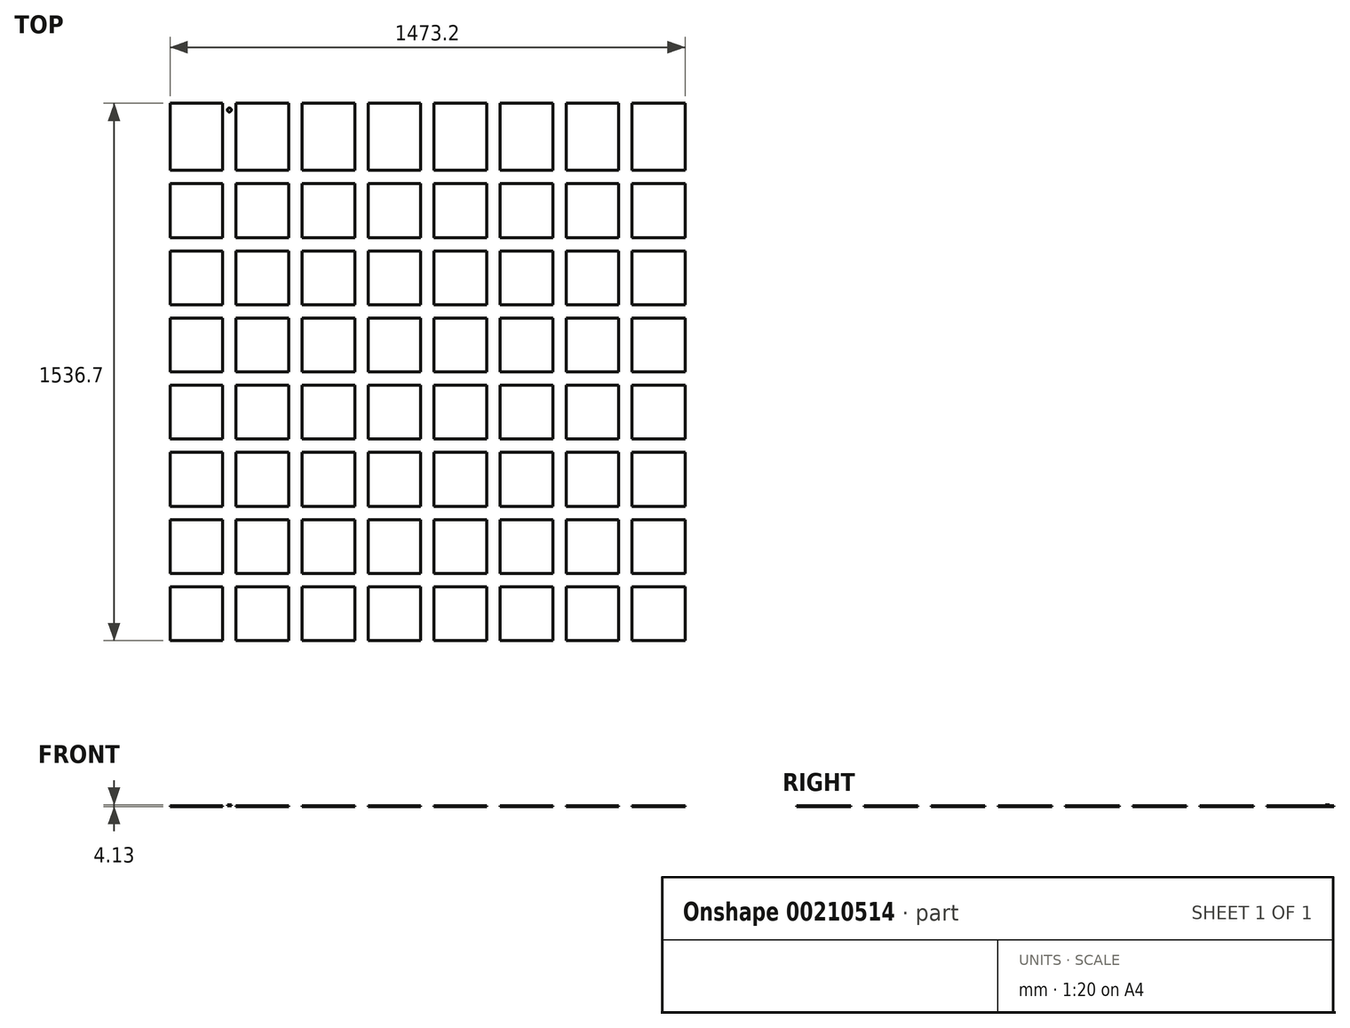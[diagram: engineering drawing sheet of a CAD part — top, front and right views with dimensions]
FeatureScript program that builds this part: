
annotation { "Feature Type Name" : "Feature", "Feature Type Description" : "" }
export const myFeature = defineFeature(function(context is Context, id is Id, definition is map)
    precondition{}
    {
        {
            var Q0;
            Q0=qCreatedBy(makeId("Top.planeOp"),FACE);
            var sketch = newSketch(context, id + "F0", { "sketchPlane" : qUnion([Q0])});
            skLineSegment(sketch, "E0.bottom", {"start": v(-755.65, 787.4) * mm, "end": v(755.65, 787.4) * mm});
            skLineSegment(sketch, "E0.top", {"start": v(-755.65, -787.4) * mm, "end": v(755.65, -787.4) * mm});
            skLineSegment(sketch, "E0.left", {"start": v(-755.65, 787.4) * mm, "end": v(-755.65, -787.4) * mm});
            skLineSegment(sketch, "E0.right", {"start": v(755.65, 787.4) * mm, "end": v(755.65, -787.4) * mm});
            skPoint(sketch, "E0.middle", {"position": v(0, 0) * mm});
            skSolve(sketch);
        }
        {
            var Q0;
            Q0=makeQuery(id+"F0.imprint","IMPRINT",FACE,{"disambiguationData":[TD([[makeQuery(id+"F0.imprint","IMPRINT",EDGE,{"derivedFrom":sQuery(id+"F0.wireOp",EDGE,"E0.bottom")}),-1.0]])]});
            extrude(context, id + "F1", {"entities" : qUnion([Q0]), "depth" : 1.59 * mm});
        }
        {
            var Q0;
            Q0=makeQuery(id+"F1.opExtrude","CAP_FACE",FACE,{"disambiguationData":[OSD([sQuery(id+"F0.wireOp",EDGE,"E0.bottom"),sQuery(id+"F0.wireOp",EDGE,"E0.top"),sQuery(id+"F0.wireOp",EDGE,"E0.left"),sQuery(id+"F0.wireOp",EDGE,"E0.right")])],"isStart":false});
            var sketch = newSketch(context, id + "F2", { "sketchPlane" : qUnion([Q0])});
            skLineSegment(sketch, "E1.bottom", {"start": v(-585.79, 787.4) * mm, "end": v(-547.69, 787.4) * mm});
            skLineSegment(sketch, "E1.top", {"start": v(-585.79, -787.4) * mm, "end": v(-547.69, -787.4) * mm});
            skLineSegment(sketch, "E1.left", {"start": v(-585.79, 787.4) * mm, "end": v(-585.79, -787.4) * mm});
            skLineSegment(sketch, "E1.right", {"start": v(-547.69, 787.4) * mm, "end": v(-547.69, -787.4) * mm});
            skLineSegment(sketch, "E2", {"start": v(-566.74, 787.4) * mm, "end": v(-566.74, -787.4) * mm, "construction": true});
            skLineSegment(sketch, "E3.1.0.0", {"start": v(-358.84, 787.4) * mm, "end": v(-358.84, -787.4) * mm});
            skLineSegment(sketch, "E3.1.0.1", {"start": v(-377.89, 787.4) * mm, "end": v(-377.89, -787.4) * mm, "construction": true});
            skLineSegment(sketch, "E3.1.0.2", {"start": v(-396.94, 787.4) * mm, "end": v(-396.94, -787.4) * mm});
            skLineSegment(sketch, "E3.2.0.0", {"start": v(-169.99, 787.4) * mm, "end": v(-169.99, -787.4) * mm});
            skLineSegment(sketch, "E3.2.0.1", {"start": v(-189.04, 787.4) * mm, "end": v(-189.04, -787.4) * mm, "construction": true});
            skLineSegment(sketch, "E3.2.0.2", {"start": v(-208.09, 787.4) * mm, "end": v(-208.09, -787.4) * mm});
            skLineSegment(sketch, "E3.3.0.0", {"start": v(18.86, 787.4) * mm, "end": v(18.86, -787.4) * mm});
            skLineSegment(sketch, "E3.3.0.1", {"start": v(-0.2, 787.4) * mm, "end": v(-0.2, -787.4) * mm, "construction": true});
            skLineSegment(sketch, "E3.3.0.2", {"start": v(-19.24, 787.4) * mm, "end": v(-19.24, -787.4) * mm});
            skLineSegment(sketch, "E3.4.0.0", {"start": v(207.7, 787.4) * mm, "end": v(207.7, -787.4) * mm});
            skLineSegment(sketch, "E3.4.0.1", {"start": v(188.66, 787.4) * mm, "end": v(188.66, -787.4) * mm, "construction": true});
            skLineSegment(sketch, "E3.4.0.2", {"start": v(169.6, 787.4) * mm, "end": v(169.6, -787.4) * mm});
            skLineSegment(sketch, "E3.5.0.0", {"start": v(396.56, 787.4) * mm, "end": v(396.56, -787.4) * mm});
            skLineSegment(sketch, "E3.5.0.1", {"start": v(377.5, 787.4) * mm, "end": v(377.5, -787.4) * mm, "construction": true});
            skLineSegment(sketch, "E3.5.0.2", {"start": v(358.46, 787.4) * mm, "end": v(358.46, -787.4) * mm});
            skLineSegment(sketch, "E3.6.0.0", {"start": v(585.4, 787.4) * mm, "end": v(585.4, -787.4) * mm});
            skLineSegment(sketch, "E3.6.0.1", {"start": v(566.36, 787.4) * mm, "end": v(566.36, -787.4) * mm, "construction": true});
            skLineSegment(sketch, "E3.6.0.2", {"start": v(547.3, 787.4) * mm, "end": v(547.3, -787.4) * mm});
            skLineSegment(sketch, "E3.direction1", {"start": v(-585.79, -787.4) * mm, "end": v(-396.94, -787.4) * mm, "construction": true});
            skLineSegment(sketch, "E4", {"start": v(736.6, 787.4) * mm, "end": v(736.6, -787.4) * mm});
            skLineSegment(sketch, "E5", {"start": v(-736.6, 787.4) * mm, "end": v(-736.6, -787.4) * mm});
            skSolve(sketch);
        }
        {
            var Q0;
            Q0=makeQuery(id+"F2.imprint","IMPRINT",FACE,{"disambiguationData":[TD([[makeQuery(id+"F2.imprint","IMPRINT",EDGE,{"derivedFrom":sQuery(id+"F2.wireOp",EDGE,"E1.bottom")}),-1.0]])]});
            var Q1;
            {var subQ0=sQuery(id+"F2.wireOp",EDGE,"E3.1.0.0");Q1=makeQuery(id+"F2.imprint","IMPRINT",FACE,{"disambiguationData":[TD([[makeQuery(id+"F2.imprint","IMPRINT",EDGE,{"derivedFrom":subQ0}),-1.0]])]});}
            var Q2;
            {var subQ0=sQuery(id+"F2.wireOp",EDGE,"E3.2.0.0");Q2=makeQuery(id+"F2.imprint","IMPRINT",FACE,{"disambiguationData":[TD([[makeQuery(id+"F2.imprint","IMPRINT",EDGE,{"derivedFrom":subQ0}),-1.0]])]});}
            var Q3;
            {var subQ0=sQuery(id+"F2.wireOp",EDGE,"E3.3.0.0");Q3=makeQuery(id+"F2.imprint","IMPRINT",FACE,{"disambiguationData":[TD([[makeQuery(id+"F2.imprint","IMPRINT",EDGE,{"derivedFrom":subQ0}),-1.0]])]});}
            var Q4;
            {var subQ0=sQuery(id+"F2.wireOp",EDGE,"E3.4.0.0");Q4=makeQuery(id+"F2.imprint","IMPRINT",FACE,{"disambiguationData":[TD([[makeQuery(id+"F2.imprint","IMPRINT",EDGE,{"derivedFrom":subQ0}),-1.0]])]});}
            var Q5;
            {var subQ0=sQuery(id+"F2.wireOp",EDGE,"E5");Q5=makeQuery(id+"F2.imprint","IMPRINT",FACE,{"disambiguationData":[TD([[makeQuery(id+"F2.imprint","IMPRINT",EDGE,{"derivedFrom":subQ0}),-1.0]])]});}
            var Q6;
            {var subQ0=sQuery(id+"F2.wireOp",EDGE,"E3.5.0.0");Q6=makeQuery(id+"F2.imprint","IMPRINT",FACE,{"disambiguationData":[TD([[makeQuery(id+"F2.imprint","IMPRINT",EDGE,{"derivedFrom":subQ0}),-1.0]])]});}
            var Q7;
            {var subQ0=sQuery(id+"F2.wireOp",EDGE,"E3.6.0.0");Q7=makeQuery(id+"F2.imprint","IMPRINT",FACE,{"disambiguationData":[TD([[makeQuery(id+"F2.imprint","IMPRINT",EDGE,{"derivedFrom":subQ0}),-1.0]])]});}
            var Q8;
            {var subQ0=sQuery(id+"F2.wireOp",EDGE,"E4");Q8=makeQuery(id+"F2.imprint","IMPRINT",FACE,{"disambiguationData":[TD([[makeQuery(id+"F2.imprint","IMPRINT",EDGE,{"derivedFrom":subQ0}),1.0]])]});}
            extrude(context, id + "F3", {"entities" : qUnion([Q0, Q1, Q2, Q3, Q4, Q5, Q6, Q7, Q8]), "depth" : 2.54 * mm});
        }
        {
            var Q0;
            {var subQ0=sQuery(id+"F2.wireOp",EDGE,"E3.2.0.0");Q0=makeQuery(id+"F2.imprint","IMPRINT",FACE,{"disambiguationData":[TD([[makeQuery(id+"F2.imprint","IMPRINT",EDGE,{"derivedFrom":subQ0}),1.0]])]});}
            var sketch = newSketch(context, id + "F4", { "sketchPlane" : qUnion([Q0])});
            skLineSegment(sketch, "E6.0.0", {"start": v(-755.65, 787.4) * mm, "end": v(-755.65, -787.4) * mm});
            skLineSegment(sketch, "E6.0.1", {"start": v(-755.65, -787.4) * mm, "end": v(755.65, -787.4) * mm});
            skLineSegment(sketch, "E6.0.2", {"start": v(755.65, -787.4) * mm, "end": v(755.65, 787.4) * mm});
            skLineSegment(sketch, "E6.0.3", {"start": v(755.65, 787.4) * mm, "end": v(-755.65, 787.4) * mm});
            skLineSegment(sketch, "E7.bottom", {"start": v(-755.65, 787.4) * mm, "end": v(755.65, 787.4) * mm});
            skLineSegment(sketch, "E7.top", {"start": v(-755.65, 749.3) * mm, "end": v(755.65, 749.3) * mm});
            skLineSegment(sketch, "E7.left", {"start": v(-755.65, 787.4) * mm, "end": v(-755.65, 749.3) * mm});
            skLineSegment(sketch, "E7.right", {"start": v(755.65, 787.4) * mm, "end": v(755.65, 749.3) * mm});
            skLineSegment(sketch, "E8", {"start": v(-755.65, 768.35) * mm, "end": v(755.65, 768.35) * mm, "construction": true});
            skLineSegment(sketch, "E9.0.1.0", {"start": v(-755.65, 557.21) * mm, "end": v(755.65, 557.21) * mm});
            skLineSegment(sketch, "E9.0.1.1", {"start": v(-755.65, 576.26) * mm, "end": v(755.65, 576.26) * mm, "construction": true});
            skLineSegment(sketch, "E9.0.1.2", {"start": v(-755.65, 595.31) * mm, "end": v(755.65, 595.31) * mm});
            skLineSegment(sketch, "E9.0.2.0", {"start": v(-755.65, 365.13) * mm, "end": v(755.65, 365.13) * mm});
            skLineSegment(sketch, "E9.0.2.1", {"start": v(-755.65, 384.18) * mm, "end": v(755.65, 384.18) * mm, "construction": true});
            skLineSegment(sketch, "E9.0.2.2", {"start": v(-755.65, 403.23) * mm, "end": v(755.65, 403.23) * mm});
            skLineSegment(sketch, "E9.0.3.0", {"start": v(-755.65, 173.04) * mm, "end": v(755.65, 173.04) * mm});
            skLineSegment(sketch, "E9.0.3.1", {"start": v(-755.65, 192.09) * mm, "end": v(755.65, 192.09) * mm, "construction": true});
            skLineSegment(sketch, "E9.0.3.2", {"start": v(-755.65, 211.14) * mm, "end": v(755.65, 211.14) * mm});
            skLineSegment(sketch, "E9.0.4.0", {"start": v(-755.65, -19.05) * mm, "end": v(755.65, -19.05) * mm});
            skLineSegment(sketch, "E9.0.4.1", {"start": v(-755.65, 0) * mm, "end": v(755.65, 0) * mm, "construction": true});
            skLineSegment(sketch, "E9.0.4.2", {"start": v(-755.65, 19.05) * mm, "end": v(755.65, 19.05) * mm});
            skLineSegment(sketch, "E9.0.5.0", {"start": v(-755.65, -211.14) * mm, "end": v(755.65, -211.14) * mm});
            skLineSegment(sketch, "E9.0.5.1", {"start": v(-755.65, -192.09) * mm, "end": v(755.65, -192.09) * mm, "construction": true});
            skLineSegment(sketch, "E9.0.5.2", {"start": v(-755.65, -173.04) * mm, "end": v(755.65, -173.04) * mm});
            skLineSegment(sketch, "E9.0.6.0", {"start": v(-755.65, -403.22) * mm, "end": v(755.65, -403.22) * mm});
            skLineSegment(sketch, "E9.0.6.1", {"start": v(-755.65, -384.17) * mm, "end": v(755.65, -384.17) * mm, "construction": true});
            skLineSegment(sketch, "E9.0.6.2", {"start": v(-755.65, -365.12) * mm, "end": v(755.65, -365.12) * mm});
            skLineSegment(sketch, "E9.0.7.0", {"start": v(-755.65, -595.31) * mm, "end": v(755.65, -595.31) * mm});
            skLineSegment(sketch, "E9.0.7.1", {"start": v(-755.65, -576.26) * mm, "end": v(755.65, -576.26) * mm, "construction": true});
            skLineSegment(sketch, "E9.0.7.2", {"start": v(-755.65, -557.21) * mm, "end": v(755.65, -557.21) * mm});
            skLineSegment(sketch, "E9.0.8.1", {"start": v(-755.65, -768.35) * mm, "end": v(755.65, -768.35) * mm, "construction": true});
            skLineSegment(sketch, "E9.0.8.2", {"start": v(-755.65, -749.3) * mm, "end": v(755.65, -749.3) * mm});
            skLineSegment(sketch, "E9.direction1", {"start": v(-755.65, 749.3) * mm, "end": v(-730.25, 749.3) * mm, "construction": true});
            skLineSegment(sketch, "E9.direction2", {"start": v(-755.65, 749.3) * mm, "end": v(-755.65, 557.21) * mm, "construction": true});
            skSolve(sketch);
        }
        {
            var Q0;
            {var subQ0=sQuery(id+"F4.wireOp",EDGE,"E6.0.1");var subQ1=sQuery(id+"F4.wireOp",EDGE,"E6.0.2");var subQ2=makeQuery(id+"F4.imprint","INTERSECT",VERTEX,{"derivedFrom":[subQ1,subQ0]});Q0=makeQuery(id+"F4.imprint","IMPRINT",FACE,{"disambiguationData":[TD([[makeQuery(id+"F4.imprint","IMPRINT",EDGE,{"disambiguationData":[TD([[subQ2,-1.0]])],"derivedFrom":subQ1}),1.0]])]});}
            var Q1;
            {var subQ0=sQuery(id+"F4.wireOp",EDGE,"E6.0.1");var subQ1=makeQuery(id+"F2.imprint","IMPRINT",EDGE,{"derivedFrom":sQuery(id+"F2.wireOp",EDGE,"E3.2.0.0")});var subQ2=makeQuery(id+"F4.imprint","INTERSECT",VERTEX,{"derivedFrom":[subQ1,subQ0]});Q1=makeQuery(id+"F4.imprint","IMPRINT",FACE,{"disambiguationData":[TD([[makeQuery(id+"F4.imprint","IMPRINT",EDGE,{"disambiguationData":[TD([[subQ2,-1.0]])],"derivedFrom":subQ0}),1.0]])]});}
            var Q2;
            {var subQ0=sQuery(id+"F4.wireOp",EDGE,"E9.0.7.0");var subQ1=sQuery(id+"F4.wireOp",EDGE,"E6.0.0");var subQ2=makeQuery(id+"F4.imprint","INTERSECT",VERTEX,{"derivedFrom":[subQ1,subQ0]});Q2=makeQuery(id+"F4.imprint","IMPRINT",FACE,{"disambiguationData":[TD([[makeQuery(id+"F4.imprint","IMPRINT",EDGE,{"disambiguationData":[TD([[subQ2,1.0]])],"derivedFrom":subQ1}),1.0]])]});}
            var Q3;
            {var subQ0=sQuery(id+"F4.wireOp",EDGE,"E9.0.7.0");var subQ1=makeQuery(id+"F2.imprint","IMPRINT",EDGE,{"derivedFrom":sQuery(id+"F2.wireOp",EDGE,"E3.2.0.0")});var subQ2=makeQuery(id+"F4.imprint","INTERSECT",VERTEX,{"derivedFrom":[subQ1,subQ0]});Q3=makeQuery(id+"F4.imprint","IMPRINT",FACE,{"disambiguationData":[TD([[makeQuery(id+"F4.imprint","IMPRINT",EDGE,{"disambiguationData":[TD([[subQ2,-1.0]])],"derivedFrom":subQ0}),1.0]])]});}
            var Q4;
            {var subQ0=sQuery(id+"F4.wireOp",EDGE,"E9.0.7.0");var subQ1=sQuery(id+"F4.wireOp",EDGE,"E6.0.2");var subQ2=makeQuery(id+"F4.imprint","INTERSECT",VERTEX,{"derivedFrom":[subQ1,subQ0]});Q4=makeQuery(id+"F4.imprint","IMPRINT",FACE,{"disambiguationData":[TD([[makeQuery(id+"F4.imprint","IMPRINT",EDGE,{"disambiguationData":[TD([[subQ2,-1.0]])],"derivedFrom":subQ1}),1.0]])]});}
            var Q5;
            {var subQ0=sQuery(id+"F4.wireOp",EDGE,"E6.0.1");var subQ1=sQuery(id+"F4.wireOp",EDGE,"E6.0.0");var subQ2=makeQuery(id+"F4.imprint","INTERSECT",VERTEX,{"derivedFrom":[subQ1,subQ0]});Q5=makeQuery(id+"F4.imprint","IMPRINT",FACE,{"disambiguationData":[TD([[makeQuery(id+"F4.imprint","IMPRINT",EDGE,{"disambiguationData":[TD([[subQ2,1.0]])],"derivedFrom":subQ1}),1.0]])]});}
            var Q6;
            {var subQ0=sQuery(id+"F4.wireOp",EDGE,"E9.0.6.0");var subQ1=sQuery(id+"F4.wireOp",EDGE,"E6.0.0");var subQ2=makeQuery(id+"F4.imprint","INTERSECT",VERTEX,{"derivedFrom":[subQ1,subQ0]});Q6=makeQuery(id+"F4.imprint","IMPRINT",FACE,{"disambiguationData":[TD([[makeQuery(id+"F4.imprint","IMPRINT",EDGE,{"disambiguationData":[TD([[subQ2,1.0]])],"derivedFrom":subQ1}),1.0]])]});}
            var Q7;
            {var subQ0=sQuery(id+"F4.wireOp",EDGE,"E9.0.6.0");var subQ1=makeQuery(id+"F2.imprint","IMPRINT",EDGE,{"derivedFrom":sQuery(id+"F2.wireOp",EDGE,"E3.2.0.0")});var subQ2=makeQuery(id+"F4.imprint","INTERSECT",VERTEX,{"derivedFrom":[subQ1,subQ0]});Q7=makeQuery(id+"F4.imprint","IMPRINT",FACE,{"disambiguationData":[TD([[makeQuery(id+"F4.imprint","IMPRINT",EDGE,{"disambiguationData":[TD([[subQ2,-1.0]])],"derivedFrom":subQ0}),1.0]])]});}
            var Q8;
            {var subQ0=sQuery(id+"F4.wireOp",EDGE,"E9.0.6.0");var subQ1=sQuery(id+"F4.wireOp",EDGE,"E6.0.2");var subQ2=makeQuery(id+"F4.imprint","INTERSECT",VERTEX,{"derivedFrom":[subQ1,subQ0]});Q8=makeQuery(id+"F4.imprint","IMPRINT",FACE,{"disambiguationData":[TD([[makeQuery(id+"F4.imprint","IMPRINT",EDGE,{"disambiguationData":[TD([[subQ2,-1.0]])],"derivedFrom":subQ1}),1.0]])]});}
            var Q9;
            {var subQ0=sQuery(id+"F4.wireOp",EDGE,"E9.0.5.0");var subQ1=sQuery(id+"F4.wireOp",EDGE,"E6.0.2");var subQ2=makeQuery(id+"F4.imprint","INTERSECT",VERTEX,{"derivedFrom":[subQ1,subQ0]});Q9=makeQuery(id+"F4.imprint","IMPRINT",FACE,{"disambiguationData":[TD([[makeQuery(id+"F4.imprint","IMPRINT",EDGE,{"disambiguationData":[TD([[subQ2,-1.0]])],"derivedFrom":subQ1}),1.0]])]});}
            var Q10;
            {var subQ0=sQuery(id+"F4.wireOp",EDGE,"E9.0.5.0");var subQ1=makeQuery(id+"F2.imprint","IMPRINT",EDGE,{"derivedFrom":sQuery(id+"F2.wireOp",EDGE,"E3.2.0.0")});var subQ2=makeQuery(id+"F4.imprint","INTERSECT",VERTEX,{"derivedFrom":[subQ1,subQ0]});Q10=makeQuery(id+"F4.imprint","IMPRINT",FACE,{"disambiguationData":[TD([[makeQuery(id+"F4.imprint","IMPRINT",EDGE,{"disambiguationData":[TD([[subQ2,-1.0]])],"derivedFrom":subQ0}),1.0]])]});}
            var Q11;
            {var subQ0=sQuery(id+"F4.wireOp",EDGE,"E9.0.5.0");var subQ1=sQuery(id+"F4.wireOp",EDGE,"E6.0.0");var subQ2=makeQuery(id+"F4.imprint","INTERSECT",VERTEX,{"derivedFrom":[subQ1,subQ0]});Q11=makeQuery(id+"F4.imprint","IMPRINT",FACE,{"disambiguationData":[TD([[makeQuery(id+"F4.imprint","IMPRINT",EDGE,{"disambiguationData":[TD([[subQ2,1.0]])],"derivedFrom":subQ1}),1.0]])]});}
            var Q12;
            {var subQ0=sQuery(id+"F4.wireOp",EDGE,"E9.0.4.0");var subQ1=sQuery(id+"F4.wireOp",EDGE,"E6.0.0");var subQ2=makeQuery(id+"F4.imprint","INTERSECT",VERTEX,{"derivedFrom":[subQ1,subQ0]});Q12=makeQuery(id+"F4.imprint","IMPRINT",FACE,{"disambiguationData":[TD([[makeQuery(id+"F4.imprint","IMPRINT",EDGE,{"disambiguationData":[TD([[subQ2,1.0]])],"derivedFrom":subQ1}),1.0]])]});}
            var Q13;
            {var subQ0=sQuery(id+"F4.wireOp",EDGE,"E9.0.4.0");var subQ1=makeQuery(id+"F2.imprint","IMPRINT",EDGE,{"derivedFrom":sQuery(id+"F2.wireOp",EDGE,"E3.2.0.0")});var subQ2=makeQuery(id+"F4.imprint","INTERSECT",VERTEX,{"derivedFrom":[subQ1,subQ0]});Q13=makeQuery(id+"F4.imprint","IMPRINT",FACE,{"disambiguationData":[TD([[makeQuery(id+"F4.imprint","IMPRINT",EDGE,{"disambiguationData":[TD([[subQ2,-1.0]])],"derivedFrom":subQ0}),1.0]])]});}
            var Q14;
            {var subQ0=sQuery(id+"F4.wireOp",EDGE,"E9.0.4.0");var subQ1=sQuery(id+"F4.wireOp",EDGE,"E6.0.2");var subQ2=makeQuery(id+"F4.imprint","INTERSECT",VERTEX,{"derivedFrom":[subQ1,subQ0]});Q14=makeQuery(id+"F4.imprint","IMPRINT",FACE,{"disambiguationData":[TD([[makeQuery(id+"F4.imprint","IMPRINT",EDGE,{"disambiguationData":[TD([[subQ2,-1.0]])],"derivedFrom":subQ1}),1.0]])]});}
            var Q15;
            {var subQ0=sQuery(id+"F4.wireOp",EDGE,"E9.0.3.0");var subQ1=sQuery(id+"F4.wireOp",EDGE,"E6.0.2");var subQ2=makeQuery(id+"F4.imprint","INTERSECT",VERTEX,{"derivedFrom":[subQ1,subQ0]});Q15=makeQuery(id+"F4.imprint","IMPRINT",FACE,{"disambiguationData":[TD([[makeQuery(id+"F4.imprint","IMPRINT",EDGE,{"disambiguationData":[TD([[subQ2,-1.0]])],"derivedFrom":subQ1}),1.0]])]});}
            var Q16;
            {var subQ0=sQuery(id+"F4.wireOp",EDGE,"E9.0.3.0");var subQ1=sQuery(id+"F4.wireOp",EDGE,"E6.0.0");var subQ2=makeQuery(id+"F4.imprint","INTERSECT",VERTEX,{"derivedFrom":[subQ1,subQ0]});Q16=makeQuery(id+"F4.imprint","IMPRINT",FACE,{"disambiguationData":[TD([[makeQuery(id+"F4.imprint","IMPRINT",EDGE,{"disambiguationData":[TD([[subQ2,1.0]])],"derivedFrom":subQ1}),1.0]])]});}
            var Q17;
            {var subQ0=sQuery(id+"F4.wireOp",EDGE,"E9.0.3.0");var subQ1=makeQuery(id+"F2.imprint","IMPRINT",EDGE,{"derivedFrom":sQuery(id+"F2.wireOp",EDGE,"E3.2.0.0")});var subQ2=makeQuery(id+"F4.imprint","INTERSECT",VERTEX,{"derivedFrom":[subQ1,subQ0]});Q17=makeQuery(id+"F4.imprint","IMPRINT",FACE,{"disambiguationData":[TD([[makeQuery(id+"F4.imprint","IMPRINT",EDGE,{"disambiguationData":[TD([[subQ2,-1.0]])],"derivedFrom":subQ0}),1.0]])]});}
            var Q18;
            {var subQ0=sQuery(id+"F4.wireOp",EDGE,"E9.0.2.0");var subQ1=sQuery(id+"F4.wireOp",EDGE,"E6.0.2");var subQ2=makeQuery(id+"F4.imprint","INTERSECT",VERTEX,{"derivedFrom":[subQ1,subQ0]});Q18=makeQuery(id+"F4.imprint","IMPRINT",FACE,{"disambiguationData":[TD([[makeQuery(id+"F4.imprint","IMPRINT",EDGE,{"disambiguationData":[TD([[subQ2,-1.0]])],"derivedFrom":subQ1}),1.0]])]});}
            var Q19;
            {var subQ0=sQuery(id+"F4.wireOp",EDGE,"E9.0.2.0");var subQ1=sQuery(id+"F4.wireOp",EDGE,"E6.0.0");var subQ2=makeQuery(id+"F4.imprint","INTERSECT",VERTEX,{"derivedFrom":[subQ1,subQ0]});Q19=makeQuery(id+"F4.imprint","IMPRINT",FACE,{"disambiguationData":[TD([[makeQuery(id+"F4.imprint","IMPRINT",EDGE,{"disambiguationData":[TD([[subQ2,1.0]])],"derivedFrom":subQ1}),1.0]])]});}
            var Q20;
            {var subQ0=sQuery(id+"F4.wireOp",EDGE,"E9.0.2.0");var subQ1=makeQuery(id+"F2.imprint","IMPRINT",EDGE,{"derivedFrom":sQuery(id+"F2.wireOp",EDGE,"E3.2.0.0")});var subQ2=makeQuery(id+"F4.imprint","INTERSECT",VERTEX,{"derivedFrom":[subQ1,subQ0]});Q20=makeQuery(id+"F4.imprint","IMPRINT",FACE,{"disambiguationData":[TD([[makeQuery(id+"F4.imprint","IMPRINT",EDGE,{"disambiguationData":[TD([[subQ2,-1.0]])],"derivedFrom":subQ0}),1.0]])]});}
            var Q21;
            {var subQ0=sQuery(id+"F4.wireOp",EDGE,"E9.0.1.0");var subQ1=sQuery(id+"F4.wireOp",EDGE,"E6.0.0");var subQ2=makeQuery(id+"F4.imprint","INTERSECT",VERTEX,{"derivedFrom":[subQ1,subQ0]});Q21=makeQuery(id+"F4.imprint","IMPRINT",FACE,{"disambiguationData":[TD([[makeQuery(id+"F4.imprint","IMPRINT",EDGE,{"disambiguationData":[TD([[subQ2,1.0]])],"derivedFrom":subQ1}),1.0]])]});}
            var Q22;
            {var subQ0=sQuery(id+"F4.wireOp",EDGE,"E9.0.1.0");var subQ1=makeQuery(id+"F2.imprint","IMPRINT",EDGE,{"derivedFrom":sQuery(id+"F2.wireOp",EDGE,"E3.2.0.0")});var subQ2=makeQuery(id+"F4.imprint","INTERSECT",VERTEX,{"derivedFrom":[subQ1,subQ0]});Q22=makeQuery(id+"F4.imprint","IMPRINT",FACE,{"disambiguationData":[TD([[makeQuery(id+"F4.imprint","IMPRINT",EDGE,{"disambiguationData":[TD([[subQ2,-1.0]])],"derivedFrom":subQ0}),1.0]])]});}
            var Q23;
            {var subQ0=sQuery(id+"F4.wireOp",EDGE,"E9.0.1.0");var subQ1=sQuery(id+"F4.wireOp",EDGE,"E6.0.2");var subQ2=makeQuery(id+"F4.imprint","INTERSECT",VERTEX,{"derivedFrom":[subQ1,subQ0]});Q23=makeQuery(id+"F4.imprint","IMPRINT",FACE,{"disambiguationData":[TD([[makeQuery(id+"F4.imprint","IMPRINT",EDGE,{"disambiguationData":[TD([[subQ2,-1.0]])],"derivedFrom":subQ1}),1.0]])]});}
            var Q24;
            {var subQ3=sQuery(id+"F4.wireOp",EDGE,"E7.right");Q24=makeQuery(id+"F4.imprint","IMPRINT",FACE,{"disambiguationData":[TD([[makeQuery(id+"F4.imprint","IMPRINT",EDGE,{"derivedFrom":subQ3}),-1.0]])]});}
            var Q25;
            {var subQ3=sQuery(id+"F4.wireOp",EDGE,"E7.left");Q25=makeQuery(id+"F4.imprint","IMPRINT",FACE,{"disambiguationData":[TD([[makeQuery(id+"F4.imprint","IMPRINT",EDGE,{"derivedFrom":subQ3}),1.0]])]});}
            var Q26;
            {var subQ0=sQuery(id+"F4.wireOp",EDGE,"E7.bottom");var subQ1=makeQuery(id+"F2.imprint","IMPRINT",EDGE,{"derivedFrom":sQuery(id+"F2.wireOp",EDGE,"E3.2.0.0")});var subQ2=makeQuery(id+"F4.imprint","INTERSECT",VERTEX,{"derivedFrom":[subQ1,subQ0]});Q26=makeQuery(id+"F4.imprint","IMPRINT",FACE,{"disambiguationData":[TD([[makeQuery(id+"F4.imprint","IMPRINT",EDGE,{"disambiguationData":[TD([[subQ2,-1.0]])],"derivedFrom":subQ0}),-1.0]])]});}
            extrude(context, id + "F5", {"entities" : qUnion([Q0, Q1, Q2, Q3, Q4, Q5, Q6, Q7, Q8, Q9, Q10, Q11, Q12, Q13, Q14, Q15, Q16, Q17, Q18, Q19, Q20, Q21, Q22, Q23, Q24, Q25, Q26]), "depth" : 2.54 * mm});
        }
        {
            var Q0;
            Q0=makeQuery(id+"F5.opExtrude","SWEPT_BODY",BODY,{"disambiguationData":[OSD([sQuery(id+"F4.wireOp",EDGE,"E7.bottom"),sQuery(id+"F4.wireOp",EDGE,"E7.top"),sQuery(id+"F4.wireOp",EDGE,"E7.left"),sQuery(id+"F4.wireOp",EDGE,"E7.right")])]});
            var Q1;
            Q1=makeQuery(id+"F3.opExtrude","SWEPT_BODY",BODY,{"disambiguationData":[OSD([sQuery(id+"F0.wireOp",EDGE,"E0.bottom"),sQuery(id+"F0.wireOp",EDGE,"E0.top"),sQuery(id+"F0.wireOp",EDGE,"E0.left"),sQuery(id+"F2.wireOp",EDGE,"E5")])]});
            var Q2;
            Q2=makeQuery(id+"F3.opExtrude","SWEPT_BODY",BODY,{"disambiguationData":[OSD([sQuery(id+"F2.wireOp",EDGE,"E1.bottom"),sQuery(id+"F2.wireOp",EDGE,"E1.top"),sQuery(id+"F2.wireOp",EDGE,"E1.left"),sQuery(id+"F2.wireOp",EDGE,"E1.right")])]});
            var Q3;
            Q3=makeQuery(id+"F3.opExtrude","SWEPT_BODY",BODY,{"disambiguationData":[OSD([sQuery(id+"F0.wireOp",EDGE,"E0.bottom"),sQuery(id+"F0.wireOp",EDGE,"E0.top"),sQuery(id+"F2.wireOp",EDGE,"E3.1.0.0"),sQuery(id+"F2.wireOp",EDGE,"E3.1.0.2")])]});
            var Q4;
            Q4=makeQuery(id+"F5.opExtrude","SWEPT_BODY",BODY,{"disambiguationData":[OSD([sQuery(id+"F4.wireOp",EDGE,"E6.0.0"),sQuery(id+"F4.wireOp",EDGE,"E6.0.2"),sQuery(id+"F4.wireOp",EDGE,"E9.0.1.0"),sQuery(id+"F4.wireOp",EDGE,"E9.0.1.2")])]});
            var Q5;
            Q5=makeQuery(id+"F3.opExtrude","SWEPT_BODY",BODY,{"disambiguationData":[OSD([sQuery(id+"F0.wireOp",EDGE,"E0.bottom"),sQuery(id+"F0.wireOp",EDGE,"E0.top"),sQuery(id+"F2.wireOp",EDGE,"E3.2.0.0"),sQuery(id+"F2.wireOp",EDGE,"E3.2.0.2")])]});
            var Q6;
            Q6=makeQuery(id+"F3.opExtrude","SWEPT_BODY",BODY,{"disambiguationData":[OSD([sQuery(id+"F0.wireOp",EDGE,"E0.bottom"),sQuery(id+"F0.wireOp",EDGE,"E0.top"),sQuery(id+"F2.wireOp",EDGE,"E3.3.0.0"),sQuery(id+"F2.wireOp",EDGE,"E3.3.0.2")])]});
            var Q7;
            Q7=makeQuery(id+"F3.opExtrude","SWEPT_BODY",BODY,{"disambiguationData":[OSD([sQuery(id+"F0.wireOp",EDGE,"E0.bottom"),sQuery(id+"F0.wireOp",EDGE,"E0.top"),sQuery(id+"F2.wireOp",EDGE,"E3.4.0.0"),sQuery(id+"F2.wireOp",EDGE,"E3.4.0.2")])]});
            var Q8;
            Q8=makeQuery(id+"F3.opExtrude","SWEPT_BODY",BODY,{"disambiguationData":[OSD([sQuery(id+"F0.wireOp",EDGE,"E0.bottom"),sQuery(id+"F0.wireOp",EDGE,"E0.top"),sQuery(id+"F2.wireOp",EDGE,"E3.5.0.0"),sQuery(id+"F2.wireOp",EDGE,"E3.5.0.2")])]});
            var Q9;
            Q9=makeQuery(id+"F3.opExtrude","SWEPT_BODY",BODY,{"disambiguationData":[OSD([sQuery(id+"F0.wireOp",EDGE,"E0.bottom"),sQuery(id+"F0.wireOp",EDGE,"E0.top"),sQuery(id+"F2.wireOp",EDGE,"E3.6.0.0"),sQuery(id+"F2.wireOp",EDGE,"E3.6.0.2")])]});
            var Q10;
            Q10=makeQuery(id+"F3.opExtrude","SWEPT_BODY",BODY,{"disambiguationData":[OSD([sQuery(id+"F0.wireOp",EDGE,"E0.bottom"),sQuery(id+"F0.wireOp",EDGE,"E0.top"),sQuery(id+"F0.wireOp",EDGE,"E0.right"),sQuery(id+"F2.wireOp",EDGE,"E4")])]});
            var Q11;
            Q11=makeQuery(id+"F5.opExtrude","SWEPT_BODY",BODY,{"disambiguationData":[OSD([sQuery(id+"F4.wireOp",EDGE,"E6.0.0"),sQuery(id+"F4.wireOp",EDGE,"E6.0.2"),sQuery(id+"F4.wireOp",EDGE,"E9.0.2.0"),sQuery(id+"F4.wireOp",EDGE,"E9.0.2.2")])]});
            var Q12;
            Q12=makeQuery(id+"F5.opExtrude","SWEPT_BODY",BODY,{"disambiguationData":[OSD([sQuery(id+"F4.wireOp",EDGE,"E6.0.0"),sQuery(id+"F4.wireOp",EDGE,"E6.0.2"),sQuery(id+"F4.wireOp",EDGE,"E9.0.3.0"),sQuery(id+"F4.wireOp",EDGE,"E9.0.3.2")])]});
            var Q13;
            Q13=makeQuery(id+"F5.opExtrude","SWEPT_BODY",BODY,{"disambiguationData":[OSD([sQuery(id+"F4.wireOp",EDGE,"E6.0.0"),sQuery(id+"F4.wireOp",EDGE,"E6.0.2"),sQuery(id+"F4.wireOp",EDGE,"E9.0.4.0"),sQuery(id+"F4.wireOp",EDGE,"E9.0.4.2")])]});
            var Q14;
            Q14=makeQuery(id+"F5.opExtrude","SWEPT_BODY",BODY,{"disambiguationData":[OSD([sQuery(id+"F4.wireOp",EDGE,"E6.0.0"),sQuery(id+"F4.wireOp",EDGE,"E6.0.2"),sQuery(id+"F4.wireOp",EDGE,"E9.0.5.0"),sQuery(id+"F4.wireOp",EDGE,"E9.0.5.2")])]});
            var Q15;
            Q15=makeQuery(id+"F5.opExtrude","SWEPT_BODY",BODY,{"disambiguationData":[OSD([sQuery(id+"F4.wireOp",EDGE,"E6.0.0"),sQuery(id+"F4.wireOp",EDGE,"E6.0.2"),sQuery(id+"F4.wireOp",EDGE,"E9.0.6.0"),sQuery(id+"F4.wireOp",EDGE,"E9.0.6.2")])]});
            var Q16;
            Q16=makeQuery(id+"F5.opExtrude","SWEPT_BODY",BODY,{"disambiguationData":[OSD([sQuery(id+"F4.wireOp",EDGE,"E6.0.0"),sQuery(id+"F4.wireOp",EDGE,"E6.0.2"),sQuery(id+"F4.wireOp",EDGE,"E9.0.7.0"),sQuery(id+"F4.wireOp",EDGE,"E9.0.7.2")])]});
            var Q17;
            Q17=makeQuery(id+"F5.opExtrude","SWEPT_BODY",BODY,{"disambiguationData":[OSD([sQuery(id+"F4.wireOp",EDGE,"E6.0.0"),sQuery(id+"F4.wireOp",EDGE,"E6.0.2"),sQuery(id+"F4.wireOp",EDGE,"E6.0.1"),sQuery(id+"F4.wireOp",EDGE,"E9.0.8.2")])]});
            booleanBodies(context, id + "F6", {"operationType" : BooleanOperationType.UNION, "tools" : qUnion([Q0, Q1, Q2, Q3, Q4, Q5, Q6, Q7, Q8, Q9, Q10, Q11, Q12, Q13, Q14, Q15, Q16, Q17])});
        }
        {
            var Q0;
            {var subQ0=sQuery(id+"F4.wireOp",EDGE,"E6.0.2");var subQ1=sQuery(id+"F4.wireOp",EDGE,"E6.0.0");var subQ2=sQuery(id+"F0.wireOp",EDGE,"E0.top");var subQ3=sQuery(id+"F0.wireOp",EDGE,"E0.bottom");Q0=makeQuery(id+"F6.opBoolean","MERGE",FACE,{"derivedFrom":[makeQuery(id+"F3.opExtrude","CAP_FACE",FACE,{"disambiguationData":[OSD([sQuery(id+"F2.wireOp",EDGE,"E1.bottom"),sQuery(id+"F2.wireOp",EDGE,"E1.top"),sQuery(id+"F2.wireOp",EDGE,"E1.left"),sQuery(id+"F2.wireOp",EDGE,"E1.right")])],"isStart":false}),makeQuery(id+"F3.opExtrude","CAP_FACE",FACE,{"disambiguationData":[OSD([subQ3,subQ2,sQuery(id+"F2.wireOp",EDGE,"E3.1.0.0"),sQuery(id+"F2.wireOp",EDGE,"E3.1.0.2")])],"isStart":false}),makeQuery(id+"F3.opExtrude","CAP_FACE",FACE,{"disambiguationData":[OSD([subQ3,subQ2,sQuery(id+"F2.wireOp",EDGE,"E3.2.0.0"),sQuery(id+"F2.wireOp",EDGE,"E3.2.0.2")])],"isStart":false}),makeQuery(id+"F3.opExtrude","CAP_FACE",FACE,{"disambiguationData":[OSD([subQ3,subQ2,sQuery(id+"F2.wireOp",EDGE,"E3.3.0.0"),sQuery(id+"F2.wireOp",EDGE,"E3.3.0.2")])],"isStart":false}),makeQuery(id+"F3.opExtrude","CAP_FACE",FACE,{"disambiguationData":[OSD([subQ3,subQ2,sQuery(id+"F2.wireOp",EDGE,"E3.4.0.0"),sQuery(id+"F2.wireOp",EDGE,"E3.4.0.2")])],"isStart":false}),makeQuery(id+"F3.opExtrude","CAP_FACE",FACE,{"disambiguationData":[OSD([subQ3,subQ2,sQuery(id+"F2.wireOp",EDGE,"E3.5.0.0"),sQuery(id+"F2.wireOp",EDGE,"E3.5.0.2")])],"isStart":false}),makeQuery(id+"F3.opExtrude","CAP_FACE",FACE,{"disambiguationData":[OSD([subQ3,subQ2,sQuery(id+"F2.wireOp",EDGE,"E3.6.0.0"),sQuery(id+"F2.wireOp",EDGE,"E3.6.0.2")])],"isStart":false}),makeQuery(id+"F3.opExtrude","CAP_FACE",FACE,{"disambiguationData":[OSD([subQ3,subQ2,sQuery(id+"F0.wireOp",EDGE,"E0.right"),sQuery(id+"F2.wireOp",EDGE,"E4")])],"isStart":false}),makeQuery(id+"F3.opExtrude","CAP_FACE",FACE,{"disambiguationData":[OSD([subQ3,subQ2,sQuery(id+"F0.wireOp",EDGE,"E0.left"),sQuery(id+"F2.wireOp",EDGE,"E5")])],"isStart":false}),makeQuery(id+"F5.opExtrude","CAP_FACE",FACE,{"disambiguationData":[OSD([subQ1,subQ0,sQuery(id+"F4.wireOp",EDGE,"E9.0.1.0"),sQuery(id+"F4.wireOp",EDGE,"E9.0.1.2")])],"isStart":false}),makeQuery(id+"F5.opExtrude","CAP_FACE",FACE,{"disambiguationData":[OSD([subQ1,subQ0,sQuery(id+"F4.wireOp",EDGE,"E9.0.2.0"),sQuery(id+"F4.wireOp",EDGE,"E9.0.2.2")])],"isStart":false}),makeQuery(id+"F5.opExtrude","CAP_FACE",FACE,{"disambiguationData":[OSD([subQ1,subQ0,sQuery(id+"F4.wireOp",EDGE,"E9.0.3.0"),sQuery(id+"F4.wireOp",EDGE,"E9.0.3.2")])],"isStart":false}),makeQuery(id+"F5.opExtrude","CAP_FACE",FACE,{"disambiguationData":[OSD([subQ1,subQ0,sQuery(id+"F4.wireOp",EDGE,"E9.0.4.0"),sQuery(id+"F4.wireOp",EDGE,"E9.0.4.2")])],"isStart":false}),makeQuery(id+"F5.opExtrude","CAP_FACE",FACE,{"disambiguationData":[OSD([subQ1,subQ0,sQuery(id+"F4.wireOp",EDGE,"E9.0.5.0"),sQuery(id+"F4.wireOp",EDGE,"E9.0.5.2")])],"isStart":false}),makeQuery(id+"F5.opExtrude","CAP_FACE",FACE,{"disambiguationData":[OSD([subQ1,subQ0,sQuery(id+"F4.wireOp",EDGE,"E9.0.6.0"),sQuery(id+"F4.wireOp",EDGE,"E9.0.6.2")])],"isStart":false}),makeQuery(id+"F5.opExtrude","CAP_FACE",FACE,{"disambiguationData":[OSD([subQ1,subQ0,sQuery(id+"F4.wireOp",EDGE,"E9.0.7.0"),sQuery(id+"F4.wireOp",EDGE,"E9.0.7.2")])],"isStart":false}),makeQuery(id+"F5.opExtrude","CAP_FACE",FACE,{"disambiguationData":[OSD([subQ1,subQ0,sQuery(id+"F4.wireOp",EDGE,"E6.0.1"),sQuery(id+"F4.wireOp",EDGE,"E9.0.8.2")])],"isStart":false}),makeQuery(id+"F5.opExtrude","CAP_FACE",FACE,{"disambiguationData":[OSD([sQuery(id+"F4.wireOp",EDGE,"E7.bottom"),sQuery(id+"F4.wireOp",EDGE,"E7.top"),sQuery(id+"F4.wireOp",EDGE,"E7.left"),sQuery(id+"F4.wireOp",EDGE,"E7.right")])],"isStart":false})]});}
            var sketch = newSketch(context, id + "F7", { "sketchPlane" : qUnion([Q0])});
            skLineSegment(sketch, "E10.0", {"start": v(-566.74, 787.4) * mm, "end": v(-566.74, -787.4) * mm});
            skCircle(sketch, "E11", {"center": v(-566.74, 768.35) * mm, "radius": 5.59 * mm});
            skCircle(sketch, "E12.1.0.0", {"center": v(-377.89, 768.35) * mm, "radius": 5.59 * mm});
            skCircle(sketch, "E12.2.0.0", {"center": v(-189.04, 768.35) * mm, "radius": 5.59 * mm});
            skCircle(sketch, "E12.3.0.0", {"center": v(-0.2, 768.35) * mm, "radius": 5.59 * mm});
            skCircle(sketch, "E12.4.0.0", {"center": v(188.66, 768.35) * mm, "radius": 5.59 * mm});
            skCircle(sketch, "E12.5.0.0", {"center": v(377.5, 768.35) * mm, "radius": 5.59 * mm});
            skCircle(sketch, "E12.6.0.0", {"center": v(566.36, 768.35) * mm, "radius": 5.59 * mm});
            skLineSegment(sketch, "E12.direction1", {"start": v(-566.74, 768.35) * mm, "end": v(-377.89, 768.35) * mm, "construction": true});
            skSolve(sketch);
        }
        {
            var Q0;
            {var subQ0=sQuery(id+"F7.wireOp",EDGE,"E11");var subQ1=sQuery(id+"F7.wireOp",EDGE,"E10.0");var subQ2=makeQuery(id+"F7.imprint","INTERSECT",VERTEX,{"disambiguationData":[OD(0.0)],"derivedFrom":[subQ1,subQ0]});Q0=makeQuery(id+"F7.imprint","IMPRINT",FACE,{"disambiguationData":[TD([[makeQuery(id+"F7.imprint","IMPRINT",EDGE,{"disambiguationData":[TD([[subQ2,-1.0]])],"derivedFrom":subQ1}),-1.0]])]});}
            var Q1;
            {var subQ0=sQuery(id+"F7.wireOp",EDGE,"E11");var subQ1=sQuery(id+"F7.wireOp",EDGE,"E10.0");var subQ2=makeQuery(id+"F7.imprint","INTERSECT",VERTEX,{"disambiguationData":[OD(0.0)],"derivedFrom":[subQ1,subQ0]});Q1=makeQuery(id+"F7.imprint","IMPRINT",FACE,{"disambiguationData":[TD([[makeQuery(id+"F7.imprint","IMPRINT",EDGE,{"disambiguationData":[TD([[subQ2,-1.0]])],"derivedFrom":subQ1}),1.0]])]});}
            var Q2;
            Q2=makeQuery(id+"F7.imprint","IMPRINT",FACE,{"disambiguationData":[TD([[makeQuery(id+"F7.imprint","IMPRINT",EDGE,{"derivedFrom":sQuery(id+"F7.wireOp",EDGE,"E12.1.0.0")}),1.0]])]});
            var Q3;
            Q3=makeQuery(id+"F7.imprint","IMPRINT",FACE,{"disambiguationData":[TD([[makeQuery(id+"F7.imprint","IMPRINT",EDGE,{"derivedFrom":sQuery(id+"F7.wireOp",EDGE,"E12.2.0.0")}),1.0]])]});
            var Q4;
            Q4=makeQuery(id+"F7.imprint","IMPRINT",FACE,{"disambiguationData":[TD([[makeQuery(id+"F7.imprint","IMPRINT",EDGE,{"derivedFrom":sQuery(id+"F7.wireOp",EDGE,"E12.3.0.0")}),1.0]])]});
            var Q5;
            Q5=makeQuery(id+"F7.imprint","IMPRINT",FACE,{"disambiguationData":[TD([[makeQuery(id+"F7.imprint","IMPRINT",EDGE,{"derivedFrom":sQuery(id+"F7.wireOp",EDGE,"E12.4.0.0")}),1.0]])]});
            var Q6;
            Q6=makeQuery(id+"F7.imprint","IMPRINT",FACE,{"disambiguationData":[TD([[makeQuery(id+"F7.imprint","IMPRINT",EDGE,{"derivedFrom":sQuery(id+"F7.wireOp",EDGE,"E12.5.0.0")}),1.0]])]});
            var Q7;
            Q7=makeQuery(id+"F7.imprint","IMPRINT",FACE,{"disambiguationData":[TD([[makeQuery(id+"F7.imprint","IMPRINT",EDGE,{"derivedFrom":sQuery(id+"F7.wireOp",EDGE,"E12.6.0.0")}),1.0]])]});
            extrude(context, id + "F8", {"entities" : qUnion([Q0, Q1, Q2, Q3, Q4, Q5, Q6, Q7]), "operationType" : NewBodyOperationType.REMOVE, "oppositeDirection" : true, "depth" : 25.4 * mm});
        }
        {
            var Q0;
            {var subQ0=sQuery(id+"F2.wireOp",EDGE,"E1.right");Q0=makeQuery(id+"F2.imprint","IMPRINT",FACE,{"disambiguationData":[TD([[makeQuery(id+"F2.imprint","IMPRINT",EDGE,{"derivedFrom":subQ0}),1.0]])]});}
            var sketch = newSketch(context, id + "F9", { "sketchPlane" : qUnion([Q0])});
            skCircle(sketch, "E13.0", {"center": v(-566.74, 768.35) * mm, "radius": 5.59 * mm});
            skCircle(sketch, "E14.0", {"center": v(-377.89, 768.35) * mm, "radius": 5.59 * mm});
            skCircle(sketch, "E15.0", {"center": v(-189.04, 768.35) * mm, "radius": 5.59 * mm});
            skCircle(sketch, "E16.0", {"center": v(-0.2, 768.35) * mm, "radius": 5.59 * mm});
            skCircle(sketch, "E17.0", {"center": v(188.66, 768.35) * mm, "radius": 5.59 * mm});
            skCircle(sketch, "E18.0", {"center": v(377.5, 768.35) * mm, "radius": 5.59 * mm});
            skCircle(sketch, "E19.0", {"center": v(566.36, 768.35) * mm, "radius": 5.59 * mm});
            skSolve(sketch);
        }
        {
            var Q0;
            Q0=makeQuery(id+"F9.imprint","IMPRINT",FACE,{"disambiguationData":[TD([[makeQuery(id+"F9.imprint","IMPRINT",EDGE,{"derivedFrom":sQuery(id+"F9.wireOp",EDGE,"E13.0")}),1.0]])]});
            var Q1;
            Q1=makeQuery(id+"F9.imprint","IMPRINT",FACE,{"disambiguationData":[TD([[makeQuery(id+"F9.imprint","IMPRINT",EDGE,{"derivedFrom":sQuery(id+"F9.wireOp",EDGE,"E14.0")}),1.0]])]});
            var Q2;
            Q2=makeQuery(id+"F9.imprint","IMPRINT",FACE,{"disambiguationData":[TD([[makeQuery(id+"F9.imprint","IMPRINT",EDGE,{"derivedFrom":sQuery(id+"F9.wireOp",EDGE,"E15.0")}),1.0]])]});
            var Q3;
            Q3=makeQuery(id+"F9.imprint","IMPRINT",FACE,{"disambiguationData":[TD([[makeQuery(id+"F9.imprint","IMPRINT",EDGE,{"derivedFrom":sQuery(id+"F9.wireOp",EDGE,"E16.0")}),1.0]])]});
            extrude(context, id + "F10", {"entities" : qUnion([Q0, Q1, Q2, Q3]), "operationType" : NewBodyOperationType.REMOVE, "endBound" : BoundingType.THROUGH_ALL, "oppositeDirection" : true, "depth" : 25.4 * mm});
        }
        {
            var Q0;
            Q0=makeQuery(id+"F0.imprint","IMPRINT",FACE,{"disambiguationData":[TD([[makeQuery(id+"F0.imprint","IMPRINT",EDGE,{"derivedFrom":sQuery(id+"F0.wireOp",EDGE,"E0.bottom")}),-1.0]])]});
            var sketch = newSketch(context, id + "F11", { "sketchPlane" : qUnion([Q0])});
            skCircle(sketch, "E20.0", {"center": v(188.66, 768.35) * mm, "radius": 5.59 * mm});
            skCircle(sketch, "E21.0", {"center": v(377.5, 768.35) * mm, "radius": 5.59 * mm});
            skCircle(sketch, "E22.0", {"center": v(566.36, 768.35) * mm, "radius": 5.59 * mm});
            skSolve(sketch);
        }
        {
            var Q0;
            Q0 = qSketchRegion(id + "F11", true);
            extrude(context, id + "F12", {"entities" : qUnion([Q0]), "operationType" : NewBodyOperationType.REMOVE, "endBound" : BoundingType.THROUGH_ALL, "depth" : 25.4 * mm});
        }
    });
